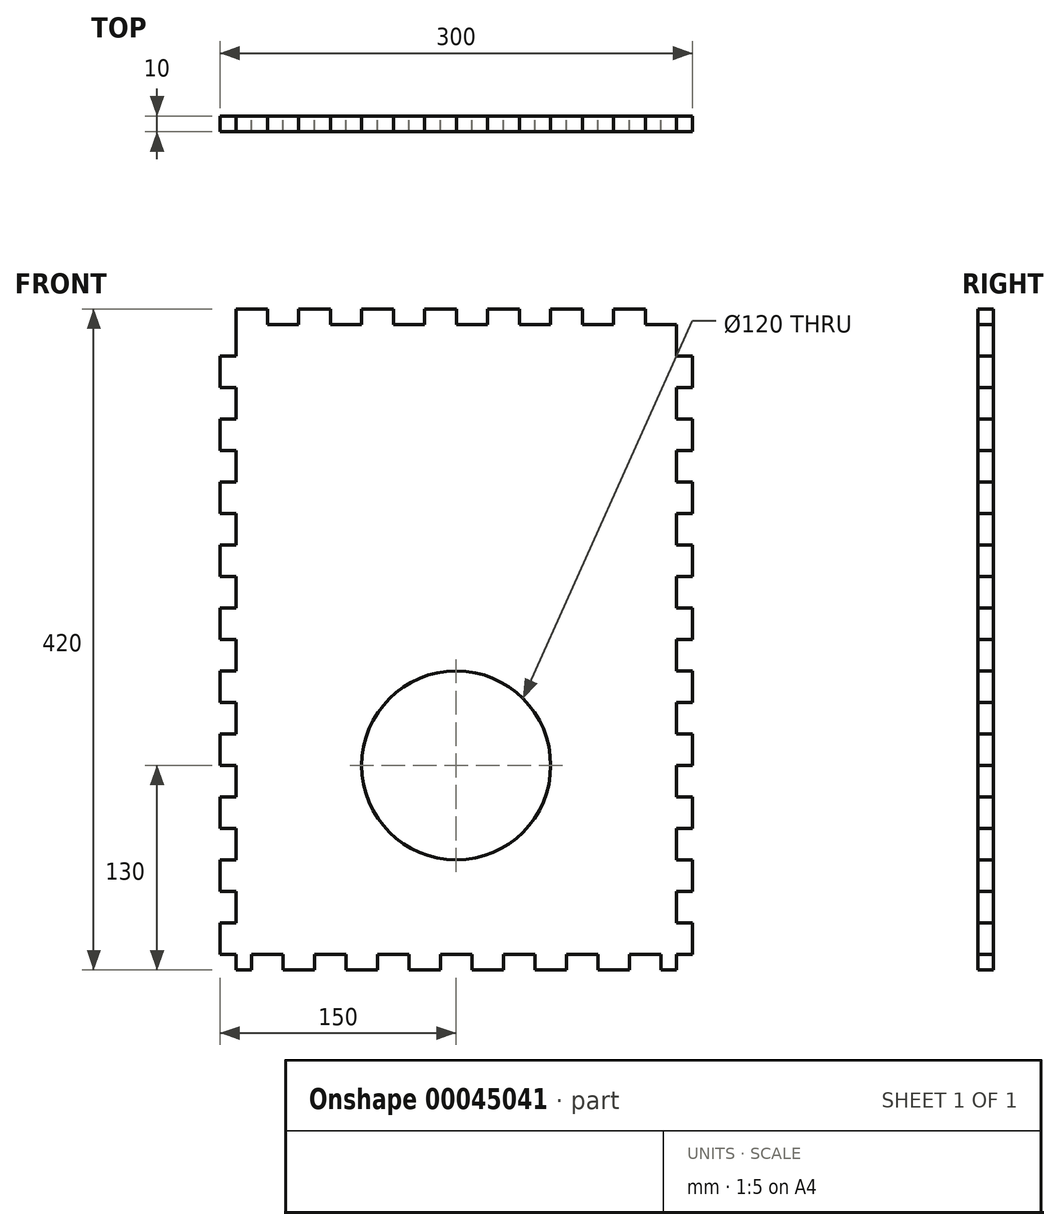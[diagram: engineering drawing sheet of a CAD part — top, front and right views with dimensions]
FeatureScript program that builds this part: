
annotation { "Feature Type Name" : "Feature", "Feature Type Description" : "" }
export const myFeature = defineFeature(function(context is Context, id is Id, definition is map)
    precondition{}
    {
        {
            var Q0;
            Q0=qCreatedBy(makeId("Front.planeOp"),FACE);
            var sketch = newSketch(context, id + "F0", { "sketchPlane" : qUnion([Q0])});
            skLineSegment(sketch, "E0.bottom", {"start": v(0, 0) * mm, "end": v(300, 0) * mm});
            skLineSegment(sketch, "E0.top", {"start": v(0, 420) * mm, "end": v(300, 420) * mm});
            skLineSegment(sketch, "E0.left", {"start": v(0, 0) * mm, "end": v(0, 420) * mm});
            skLineSegment(sketch, "E0.right", {"start": v(300, 0) * mm, "end": v(300, 420) * mm});
            skSolve(sketch);
        }
        {
            var Q0;
            Q0 = qSketchRegion(id + "F0", true);
            extrude(context, id + "F1", {"entities" : qUnion([Q0]), "depth" : 10 * mm});
        }
        {
            var Q0;
            Q0=makeQuery(id+"F1.opExtrude","CAP_FACE",FACE,{"disambiguationData":[OSD([sQuery(id+"F0.wireOp",EDGE,"E0.bottom"),sQuery(id+"F0.wireOp",EDGE,"E0.top"),sQuery(id+"F0.wireOp",EDGE,"E0.left"),sQuery(id+"F0.wireOp",EDGE,"E0.right")])],"isStart":true});
            var sketch = newSketch(context, id + "F2", { "sketchPlane" : qUnion([Q0])});
            skLineSegment(sketch, "E1.bottom", {"start": v(-300, 0) * mm, "end": v(-290, 0) * mm});
            skLineSegment(sketch, "E1.top", {"start": v(-300, 10) * mm, "end": v(-290, 10) * mm});
            skLineSegment(sketch, "E1.left", {"start": v(-300, 0) * mm, "end": v(-300, 10) * mm});
            skLineSegment(sketch, "E1.right", {"start": v(-290, 0) * mm, "end": v(-290, 10) * mm});
            skLineSegment(sketch, "E2.bottom", {"start": v(-280, 0) * mm, "end": v(-260.07, 0) * mm});
            skLineSegment(sketch, "E2.top", {"start": v(-280, 10) * mm, "end": v(-260.07, 10) * mm});
            skLineSegment(sketch, "E2.left", {"start": v(-280, 0) * mm, "end": v(-280, 10) * mm});
            skLineSegment(sketch, "E2.right", {"start": v(-260.07, 0) * mm, "end": v(-260.07, 10) * mm});
            skLineSegment(sketch, "E3.1.0.0", {"start": v(-220.07, 0) * mm, "end": v(-220.07, 10) * mm});
            skLineSegment(sketch, "E3.1.0.1", {"start": v(-240, 0) * mm, "end": v(-220.07, 0) * mm});
            skLineSegment(sketch, "E3.1.0.2", {"start": v(-240, 10) * mm, "end": v(-220.07, 10) * mm});
            skLineSegment(sketch, "E3.1.0.3", {"start": v(-240, 0) * mm, "end": v(-240, 10) * mm});
            skLineSegment(sketch, "E3.2.0.0", {"start": v(-180.07, 0) * mm, "end": v(-180.07, 10) * mm});
            skLineSegment(sketch, "E3.2.0.1", {"start": v(-200, 0) * mm, "end": v(-180.07, 0) * mm});
            skLineSegment(sketch, "E3.2.0.2", {"start": v(-200, 10) * mm, "end": v(-180.07, 10) * mm});
            skLineSegment(sketch, "E3.2.0.3", {"start": v(-200, 0) * mm, "end": v(-200, 10) * mm});
            skLineSegment(sketch, "E3.3.0.0", {"start": v(-140.07, 0) * mm, "end": v(-140.07, 10) * mm});
            skLineSegment(sketch, "E3.3.0.1", {"start": v(-160, 0) * mm, "end": v(-140.07, 0) * mm});
            skLineSegment(sketch, "E3.3.0.2", {"start": v(-160, 10) * mm, "end": v(-140.07, 10) * mm});
            skLineSegment(sketch, "E3.3.0.3", {"start": v(-160, 0) * mm, "end": v(-160, 10) * mm});
            skLineSegment(sketch, "E3.4.0.0", {"start": v(-100.07, 0) * mm, "end": v(-100.07, 10) * mm});
            skLineSegment(sketch, "E3.4.0.1", {"start": v(-120, 0) * mm, "end": v(-100.07, 0) * mm});
            skLineSegment(sketch, "E3.4.0.2", {"start": v(-120, 10) * mm, "end": v(-100.07, 10) * mm});
            skLineSegment(sketch, "E3.4.0.3", {"start": v(-120, 0) * mm, "end": v(-120, 10) * mm});
            skLineSegment(sketch, "E3.5.0.0", {"start": v(-60.07, 0) * mm, "end": v(-60.07, 10) * mm});
            skLineSegment(sketch, "E3.5.0.1", {"start": v(-80, 0) * mm, "end": v(-60.07, 0) * mm});
            skLineSegment(sketch, "E3.5.0.2", {"start": v(-80, 10) * mm, "end": v(-60.07, 10) * mm});
            skLineSegment(sketch, "E3.5.0.3", {"start": v(-80, 0) * mm, "end": v(-80, 10) * mm});
            skLineSegment(sketch, "E3.6.0.0", {"start": v(-20.07, 0) * mm, "end": v(-20.07, 10) * mm});
            skLineSegment(sketch, "E3.6.0.1", {"start": v(-40, 0) * mm, "end": v(-20.07, 0) * mm});
            skLineSegment(sketch, "E3.6.0.2", {"start": v(-40, 10) * mm, "end": v(-20.07, 10) * mm});
            skLineSegment(sketch, "E3.6.0.3", {"start": v(-40, 0) * mm, "end": v(-40, 10) * mm});
            skLineSegment(sketch, "E3.direction1", {"start": v(-260.07, 0) * mm, "end": v(-220.07, 0) * mm, "construction": true});
            skLineSegment(sketch, "E4.bottom", {"start": v(0, 0) * mm, "end": v(-10, 0) * mm});
            skLineSegment(sketch, "E4.top", {"start": v(0, 10) * mm, "end": v(-10, 10) * mm});
            skLineSegment(sketch, "E4.left", {"start": v(0, 0) * mm, "end": v(0, 10) * mm});
            skLineSegment(sketch, "E4.right", {"start": v(-10, 0) * mm, "end": v(-10, 10) * mm});
            skLineSegment(sketch, "E5.bottom", {"start": v(-300, 30.07) * mm, "end": v(-290, 30.07) * mm});
            skLineSegment(sketch, "E5.top", {"start": v(-300, 50) * mm, "end": v(-290, 50) * mm});
            skLineSegment(sketch, "E5.left", {"start": v(-300, 30.07) * mm, "end": v(-300, 50) * mm});
            skLineSegment(sketch, "E5.right", {"start": v(-290, 30.07) * mm, "end": v(-290, 50) * mm});
            skLineSegment(sketch, "E6.0.1.0", {"start": v(-300, 70.08) * mm, "end": v(-290, 70.08) * mm});
            skLineSegment(sketch, "E6.0.1.1", {"start": v(-290, 70.08) * mm, "end": v(-290, 90) * mm});
            skLineSegment(sketch, "E6.0.1.2", {"start": v(-300, 90) * mm, "end": v(-290, 90) * mm});
            skLineSegment(sketch, "E6.0.1.3", {"start": v(-300, 70.08) * mm, "end": v(-300, 90) * mm});
            skLineSegment(sketch, "E6.0.2.0", {"start": v(-300, 110.07) * mm, "end": v(-290, 110.07) * mm});
            skLineSegment(sketch, "E6.0.2.1", {"start": v(-290, 110.07) * mm, "end": v(-290, 130) * mm});
            skLineSegment(sketch, "E6.0.2.2", {"start": v(-300, 130) * mm, "end": v(-290, 130) * mm});
            skLineSegment(sketch, "E6.0.2.3", {"start": v(-300, 110.07) * mm, "end": v(-300, 130) * mm});
            skLineSegment(sketch, "E6.0.3.0", {"start": v(-300, 150.07) * mm, "end": v(-290, 150.07) * mm});
            skLineSegment(sketch, "E6.0.3.1", {"start": v(-290, 150.07) * mm, "end": v(-290, 170) * mm});
            skLineSegment(sketch, "E6.0.3.2", {"start": v(-300, 170) * mm, "end": v(-290, 170) * mm});
            skLineSegment(sketch, "E6.0.3.3", {"start": v(-300, 150.07) * mm, "end": v(-300, 170) * mm});
            skLineSegment(sketch, "E6.0.4.0", {"start": v(-300, 190.07) * mm, "end": v(-290, 190.07) * mm});
            skLineSegment(sketch, "E6.0.4.1", {"start": v(-290, 190.07) * mm, "end": v(-290, 210) * mm});
            skLineSegment(sketch, "E6.0.4.2", {"start": v(-300, 210) * mm, "end": v(-290, 210) * mm});
            skLineSegment(sketch, "E6.0.4.3", {"start": v(-300, 190.07) * mm, "end": v(-300, 210) * mm});
            skLineSegment(sketch, "E6.0.5.0", {"start": v(-300, 230.07) * mm, "end": v(-290, 230.07) * mm});
            skLineSegment(sketch, "E6.0.5.1", {"start": v(-290, 230.07) * mm, "end": v(-290, 250) * mm});
            skLineSegment(sketch, "E6.0.5.2", {"start": v(-300, 250) * mm, "end": v(-290, 250) * mm});
            skLineSegment(sketch, "E6.0.5.3", {"start": v(-300, 230.07) * mm, "end": v(-300, 250) * mm});
            skLineSegment(sketch, "E6.0.6.0", {"start": v(-300, 270.07) * mm, "end": v(-290, 270.07) * mm});
            skLineSegment(sketch, "E6.0.6.1", {"start": v(-290, 270.07) * mm, "end": v(-290, 290) * mm});
            skLineSegment(sketch, "E6.0.6.2", {"start": v(-300, 290) * mm, "end": v(-290, 290) * mm});
            skLineSegment(sketch, "E6.0.6.3", {"start": v(-300, 270.07) * mm, "end": v(-300, 290) * mm});
            skLineSegment(sketch, "E6.0.7.0", {"start": v(-300, 310.07) * mm, "end": v(-290, 310.07) * mm});
            skLineSegment(sketch, "E6.0.7.1", {"start": v(-290, 310.07) * mm, "end": v(-290, 330) * mm});
            skLineSegment(sketch, "E6.0.7.2", {"start": v(-300, 330) * mm, "end": v(-290, 330) * mm});
            skLineSegment(sketch, "E6.0.7.3", {"start": v(-300, 310.07) * mm, "end": v(-300, 330) * mm});
            skLineSegment(sketch, "E6.0.8.0", {"start": v(-300, 350.07) * mm, "end": v(-290, 350.07) * mm});
            skLineSegment(sketch, "E6.0.8.1", {"start": v(-290, 350.07) * mm, "end": v(-290, 370) * mm});
            skLineSegment(sketch, "E6.0.8.2", {"start": v(-300, 370) * mm, "end": v(-290, 370) * mm});
            skLineSegment(sketch, "E6.0.8.3", {"start": v(-300, 350.07) * mm, "end": v(-300, 370) * mm});
            skLineSegment(sketch, "E6.0.9.0", {"start": v(-300, 390.07) * mm, "end": v(-290, 390.07) * mm});
            skLineSegment(sketch, "E6.0.9.1", {"start": v(-290, 390.07) * mm, "end": v(-290, 410) * mm});
            skLineSegment(sketch, "E6.0.9.2", {"start": v(-300, 410) * mm, "end": v(-290, 410) * mm});
            skLineSegment(sketch, "E6.0.9.3", {"start": v(-300, 390.07) * mm, "end": v(-300, 410) * mm});
            skLineSegment(sketch, "E6.direction1", {"start": v(-300, 30.07) * mm, "end": v(-275, 30.07) * mm, "construction": true});
            skLineSegment(sketch, "E6.direction2", {"start": v(-300, 30.07) * mm, "end": v(-300, 70.08) * mm, "construction": true});
            skLineSegment(sketch, "E7.bottom", {"start": v(-290, 410) * mm, "end": v(-300, 410) * mm});
            skLineSegment(sketch, "E7.top", {"start": v(-290, 420) * mm, "end": v(-300, 420) * mm});
            skLineSegment(sketch, "E7.left", {"start": v(-290, 410) * mm, "end": v(-290, 420) * mm});
            skLineSegment(sketch, "E7.right", {"start": v(-300, 410) * mm, "end": v(-300, 420) * mm});
            skLineSegment(sketch, "E8.bottom", {"start": v(-290, 410) * mm, "end": v(-270.08, 410) * mm});
            skLineSegment(sketch, "E8.top", {"start": v(-290, 420) * mm, "end": v(-270.08, 420) * mm});
            skLineSegment(sketch, "E8.right", {"start": v(-270.08, 410) * mm, "end": v(-270.08, 420) * mm});
            skLineSegment(sketch, "E9.1.0.0", {"start": v(-250, 420) * mm, "end": v(-230.08, 420) * mm});
            skLineSegment(sketch, "E9.1.0.1", {"start": v(-250, 410) * mm, "end": v(-250, 420) * mm});
            skLineSegment(sketch, "E9.1.0.2", {"start": v(-230.08, 410) * mm, "end": v(-230.08, 420) * mm});
            skLineSegment(sketch, "E9.1.0.3", {"start": v(-250, 410) * mm, "end": v(-230.08, 410) * mm});
            skLineSegment(sketch, "E9.2.0.0", {"start": v(-210, 420) * mm, "end": v(-190.08, 420) * mm});
            skLineSegment(sketch, "E9.2.0.1", {"start": v(-210, 410) * mm, "end": v(-210, 420) * mm});
            skLineSegment(sketch, "E9.2.0.2", {"start": v(-190.08, 410) * mm, "end": v(-190.08, 420) * mm});
            skLineSegment(sketch, "E9.2.0.3", {"start": v(-210, 410) * mm, "end": v(-190.08, 410) * mm});
            skLineSegment(sketch, "E9.3.0.0", {"start": v(-170, 420) * mm, "end": v(-150.08, 420) * mm});
            skLineSegment(sketch, "E9.3.0.1", {"start": v(-170, 410) * mm, "end": v(-170, 420) * mm});
            skLineSegment(sketch, "E9.3.0.2", {"start": v(-150.08, 410) * mm, "end": v(-150.08, 420) * mm});
            skLineSegment(sketch, "E9.3.0.3", {"start": v(-170, 410) * mm, "end": v(-150.08, 410) * mm});
            skLineSegment(sketch, "E9.4.0.0", {"start": v(-130, 420) * mm, "end": v(-110.08, 420) * mm});
            skLineSegment(sketch, "E9.4.0.1", {"start": v(-130, 410) * mm, "end": v(-130, 420) * mm});
            skLineSegment(sketch, "E9.4.0.2", {"start": v(-110.08, 410) * mm, "end": v(-110.08, 420) * mm});
            skLineSegment(sketch, "E9.4.0.3", {"start": v(-130, 410) * mm, "end": v(-110.08, 410) * mm});
            skLineSegment(sketch, "E9.5.0.0", {"start": v(-90, 420) * mm, "end": v(-70.08, 420) * mm});
            skLineSegment(sketch, "E9.5.0.1", {"start": v(-90, 410) * mm, "end": v(-90, 420) * mm});
            skLineSegment(sketch, "E9.5.0.2", {"start": v(-70.08, 410) * mm, "end": v(-70.08, 420) * mm});
            skLineSegment(sketch, "E9.5.0.3", {"start": v(-90, 410) * mm, "end": v(-70.08, 410) * mm});
            skLineSegment(sketch, "E9.6.0.0", {"start": v(-50, 420) * mm, "end": v(-30.08, 420) * mm});
            skLineSegment(sketch, "E9.6.0.1", {"start": v(-50, 410) * mm, "end": v(-50, 420) * mm});
            skLineSegment(sketch, "E9.6.0.2", {"start": v(-30.08, 410) * mm, "end": v(-30.08, 420) * mm});
            skLineSegment(sketch, "E9.6.0.3", {"start": v(-50, 410) * mm, "end": v(-30.08, 410) * mm});
            skLineSegment(sketch, "E9.direction1", {"start": v(-290, 420) * mm, "end": v(-250, 420) * mm, "construction": true});
            skLineSegment(sketch, "E10.0.7.0", {"start": v(-10, 420) * mm, "end": v(9.92, 420) * mm});
            skLineSegment(sketch, "E10.3.7.0", {"start": v(-10, 410) * mm, "end": v(-10, 420) * mm});
            skLineSegment(sketch, "E10.6.7.0", {"start": v(9.92, 410) * mm, "end": v(9.92, 420) * mm});
            skLineSegment(sketch, "E10.9.7.0", {"start": v(-10, 410) * mm, "end": v(9.92, 410) * mm});
            skLineSegment(sketch, "E11.bottom", {"start": v(-10, 410) * mm, "end": v(0, 410) * mm});
            skLineSegment(sketch, "E11.top", {"start": v(-10, 390.07) * mm, "end": v(0, 390.07) * mm});
            skLineSegment(sketch, "E11.left", {"start": v(-10, 410) * mm, "end": v(-10, 390.07) * mm});
            skLineSegment(sketch, "E11.right", {"start": v(0, 410) * mm, "end": v(0, 390.07) * mm});
            skLineSegment(sketch, "E12.0.1.0", {"start": v(-10, 370) * mm, "end": v(0, 370) * mm});
            skLineSegment(sketch, "E12.0.1.1", {"start": v(0, 370) * mm, "end": v(0, 350.07) * mm});
            skLineSegment(sketch, "E12.0.1.2", {"start": v(-10, 370) * mm, "end": v(-10, 350.07) * mm});
            skLineSegment(sketch, "E12.0.1.3", {"start": v(-10, 350.07) * mm, "end": v(0, 350.07) * mm});
            skLineSegment(sketch, "E12.0.2.0", {"start": v(-10, 330) * mm, "end": v(0, 330) * mm});
            skLineSegment(sketch, "E12.0.2.1", {"start": v(0, 330) * mm, "end": v(0, 310.07) * mm});
            skLineSegment(sketch, "E12.0.2.2", {"start": v(-10, 330) * mm, "end": v(-10, 310.07) * mm});
            skLineSegment(sketch, "E12.0.2.3", {"start": v(-10, 310.07) * mm, "end": v(0, 310.07) * mm});
            skLineSegment(sketch, "E12.0.3.0", {"start": v(-10, 290) * mm, "end": v(0, 290) * mm});
            skLineSegment(sketch, "E12.0.3.1", {"start": v(0, 290) * mm, "end": v(0, 270.07) * mm});
            skLineSegment(sketch, "E12.0.3.2", {"start": v(-10, 290) * mm, "end": v(-10, 270.07) * mm});
            skLineSegment(sketch, "E12.0.3.3", {"start": v(-10, 270.07) * mm, "end": v(0, 270.07) * mm});
            skLineSegment(sketch, "E12.0.4.0", {"start": v(-10, 250) * mm, "end": v(0, 250) * mm});
            skLineSegment(sketch, "E12.0.4.1", {"start": v(0, 250) * mm, "end": v(0, 230.07) * mm});
            skLineSegment(sketch, "E12.0.4.2", {"start": v(-10, 250) * mm, "end": v(-10, 230.07) * mm});
            skLineSegment(sketch, "E12.0.4.3", {"start": v(-10, 230.07) * mm, "end": v(0, 230.07) * mm});
            skLineSegment(sketch, "E12.0.5.0", {"start": v(-10, 210) * mm, "end": v(0, 210) * mm});
            skLineSegment(sketch, "E12.0.5.1", {"start": v(0, 210) * mm, "end": v(0, 190.07) * mm});
            skLineSegment(sketch, "E12.0.5.2", {"start": v(-10, 210) * mm, "end": v(-10, 190.07) * mm});
            skLineSegment(sketch, "E12.0.5.3", {"start": v(-10, 190.07) * mm, "end": v(0, 190.07) * mm});
            skLineSegment(sketch, "E12.0.6.0", {"start": v(-10, 170) * mm, "end": v(0, 170) * mm});
            skLineSegment(sketch, "E12.0.6.1", {"start": v(0, 170) * mm, "end": v(0, 150.08) * mm});
            skLineSegment(sketch, "E12.0.6.2", {"start": v(-10, 170) * mm, "end": v(-10, 150.08) * mm});
            skLineSegment(sketch, "E12.0.6.3", {"start": v(-10, 150.08) * mm, "end": v(0, 150.08) * mm});
            skLineSegment(sketch, "E12.0.7.0", {"start": v(-10, 130) * mm, "end": v(0, 130) * mm});
            skLineSegment(sketch, "E12.0.7.1", {"start": v(0, 130) * mm, "end": v(0, 110.08) * mm});
            skLineSegment(sketch, "E12.0.7.2", {"start": v(-10, 130) * mm, "end": v(-10, 110.08) * mm});
            skLineSegment(sketch, "E12.0.7.3", {"start": v(-10, 110.08) * mm, "end": v(0, 110.08) * mm});
            skLineSegment(sketch, "E12.0.8.0", {"start": v(-10, 90) * mm, "end": v(0, 90) * mm});
            skLineSegment(sketch, "E12.0.8.1", {"start": v(0, 90) * mm, "end": v(0, 70.08) * mm});
            skLineSegment(sketch, "E12.0.8.2", {"start": v(-10, 90) * mm, "end": v(-10, 70.08) * mm});
            skLineSegment(sketch, "E12.0.8.3", {"start": v(-10, 70.08) * mm, "end": v(0, 70.08) * mm});
            skLineSegment(sketch, "E12.0.9.0", {"start": v(-10, 50) * mm, "end": v(0, 50) * mm});
            skLineSegment(sketch, "E12.0.9.1", {"start": v(0, 50) * mm, "end": v(0, 30.08) * mm});
            skLineSegment(sketch, "E12.0.9.2", {"start": v(-10, 50) * mm, "end": v(-10, 30.08) * mm});
            skLineSegment(sketch, "E12.0.9.3", {"start": v(-10, 30.08) * mm, "end": v(0, 30.08) * mm});
            skLineSegment(sketch, "E12.direction1", {"start": v(-10, 410) * mm, "end": v(15, 410) * mm, "construction": true});
            skLineSegment(sketch, "E12.direction2", {"start": v(-10, 410) * mm, "end": v(-10, 370) * mm, "construction": true});
            skSolve(sketch);
        }
        {
            var Q0;
            Q0 = qSketchRegion(id + "F2", true);
            extrude(context, id + "F3", {"entities" : qUnion([Q0]), "operationType" : NewBodyOperationType.REMOVE, "endBound" : BoundingType.THROUGH_ALL, "oppositeDirection" : true, "depth" : 25 * mm});
        }
        {
            var Q0;
            Q0=makeQuery(id+"F1.opExtrude","CAP_FACE",FACE,{"disambiguationData":[OSD([sQuery(id+"F0.wireOp",EDGE,"E0.bottom"),sQuery(id+"F0.wireOp",EDGE,"E0.top"),sQuery(id+"F0.wireOp",EDGE,"E0.left"),sQuery(id+"F0.wireOp",EDGE,"E0.right")])],"isStart":true});
            var sketch = newSketch(context, id + "F4", { "sketchPlane" : qUnion([Q0])});
            skCircle(sketch, "E13", {"center": v(-150, 130) * mm, "radius": 60 * mm});
            skSolve(sketch);
        }
        {
            var Q0;
            Q0 = qSketchRegion(id + "F4", true);
            extrude(context, id + "F5", {"entities" : qUnion([Q0]), "operationType" : NewBodyOperationType.REMOVE, "endBound" : BoundingType.THROUGH_ALL, "oppositeDirection" : true, "depth" : 25 * mm});
        }
    });
